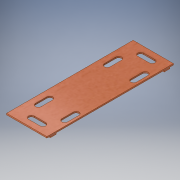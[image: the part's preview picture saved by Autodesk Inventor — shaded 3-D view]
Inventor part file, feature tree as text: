
AUTODESK INVENTOR PART (.ipt)
format: ipt  version: 2018 (Build 220112000, 112)  size: 199,168 bytes
history: native  units: mm
features: extrude x2, sketch x2, projected_geometry x1
ambient origin geometry x8: Origin, YZ Plane, XZ Plane, XY Plane, X Axis, Y Axis, Z Axis, Center Point
bodies: Body1 (feature_tree)
feature tree (5):
  extrude  "Extrusion2"  Depth=110.0mm
  extrude  "Extrusion3"  Depth=10.0mm
  sketch  "Skizze1"  dims[d0=35.0mm d1=110.0mm]
  sketch  "Skizze2"  dims[d4=10.0mm d5=10.0mm d6=10.0mm d7=5.0mm d8=5.0mm d9=5.0mm d10=5.0mm d11=5.0mm d12=2.0mm d13=5.0mm d14=50.0mm d15=5.0mm d16=1.2mm d17=0.0mm d18=5.0mm d19=5.0mm d20=5.0mm d21=5.0mm d22=3.0mm d23=0.0mm d24=3.0mm d25=3.0mm d26=1.2mm d27=0.0mm]
  projected_geometry  "Projizierte Kontur1"
